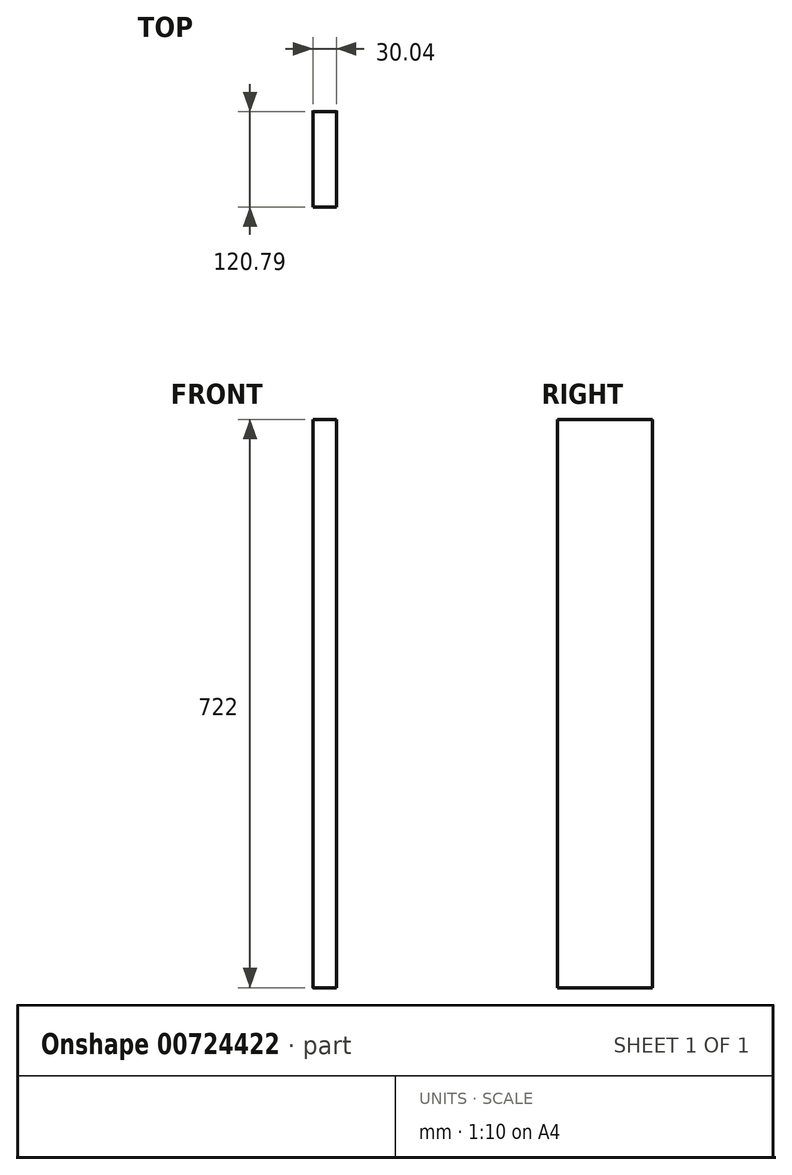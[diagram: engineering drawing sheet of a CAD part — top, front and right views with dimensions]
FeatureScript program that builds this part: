
annotation { "Feature Type Name" : "Feature", "Feature Type Description" : "" }
export const myFeature = defineFeature(function(context is Context, id is Id, definition is map)
    precondition{}
    {
        {
            var Q0;
            Q0=qCreatedBy(makeId("Top.planeOp"),FACE);
            var sketch = newSketch(context, id + "F0", { "sketchPlane" : qUnion([Q0])});
            skLineSegment(sketch, "E0", {"start": v(0, 0) * mm, "end": v(200000, 0) * mm, "construction": true});
            skLineSegment(sketch, "E1", {"start": v(0, 0) * mm, "end": v(199999.96, 120.78) * mm, "construction": true});
            skArc(sketch, "E2", {"start": v(199999.96, 120.78) * mm, "mid": v(200000, 60.39) * mm, "end": v(200000, 0) * mm});
            skArc(sketch, "E3.0", {"start": v(200029.96, 120.8) * mm, "mid": v(200030, 60.4) * mm, "end": v(200030, 0) * mm});
            skLineSegment(sketch, "E4", {"start": v(200000, 0) * mm, "end": v(200030, 0) * mm});
            skLineSegment(sketch, "E5", {"start": v(199999.96, 120.78) * mm, "end": v(200029.96, 120.8) * mm});
            skSolve(sketch);
        }
        {
            var Q0;
            Q0 = qSketchRegion(id + "F0", true);
            var Q1;
            Q1 = qConstructionFilter(qBodyType(qCreatedBy(id + "F0" ,EDGE), BodyType.WIRE), ConstructionObject.NO);
            extrude(context, id + "F1", {"entities" : qUnion([Q0]), "surfaceEntities" : qUnion([Q1]), "depth" : 722 * mm, "offsetDistance" : 25 * mm});
        }
    });
